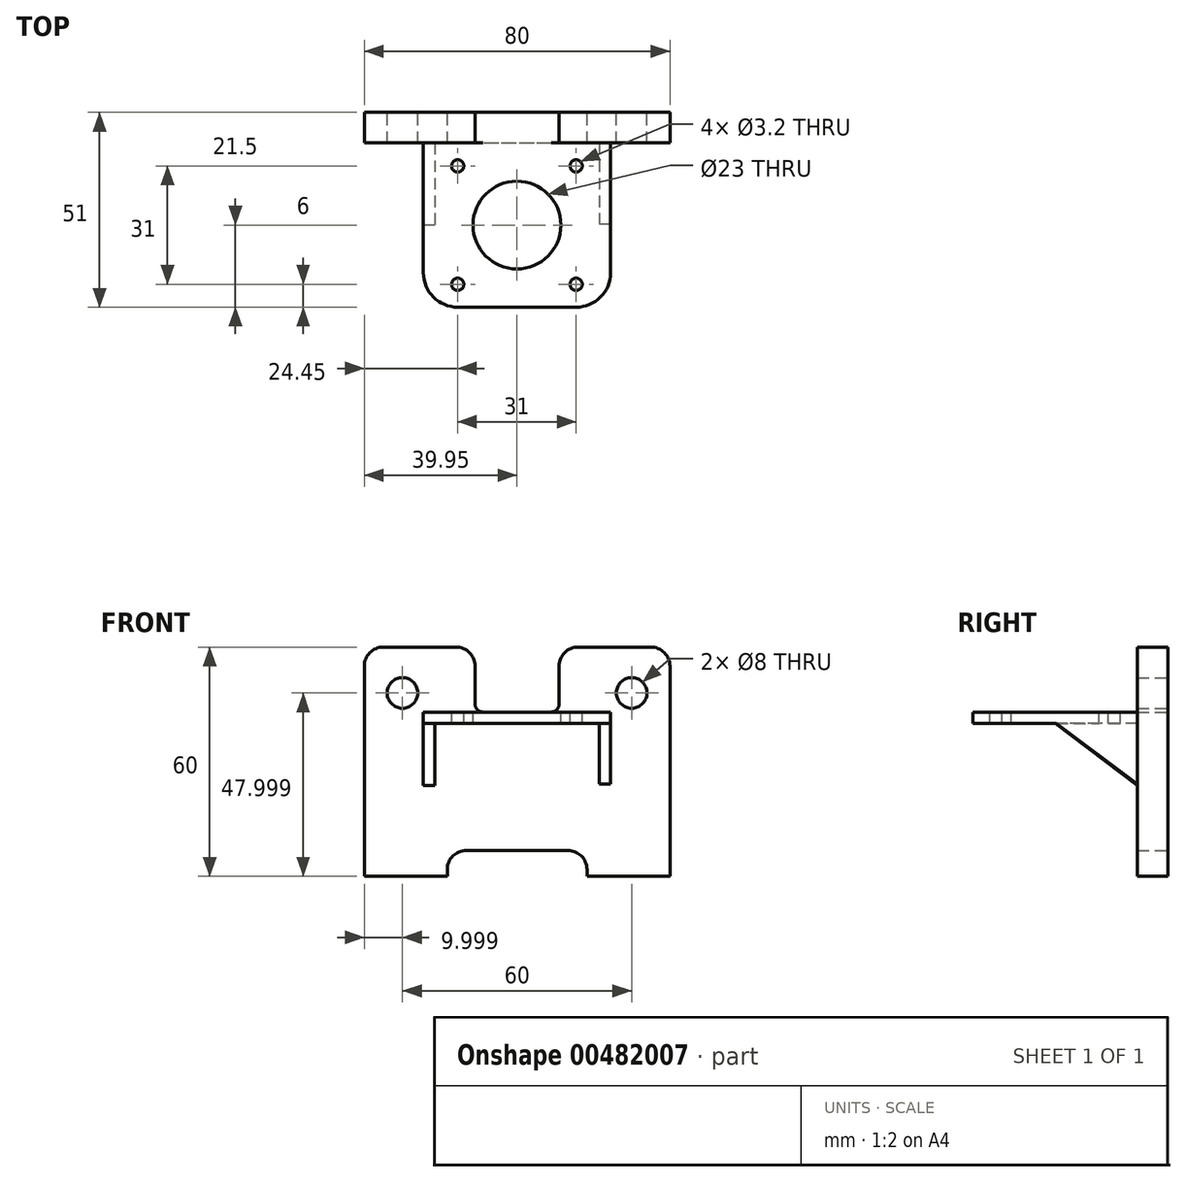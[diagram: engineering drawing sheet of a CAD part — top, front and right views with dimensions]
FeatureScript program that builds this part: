
annotation { "Feature Type Name" : "Feature", "Feature Type Description" : "" }
export const myFeature = defineFeature(function(context is Context, id is Id, definition is map)
    precondition{}
    {
        {
            var Q0;
            Q0=qCreatedBy(makeId("Front.planeOp"),FACE);
            var sketch = newSketch(context, id + "F0", { "sketchPlane" : qUnion([Q0])});
            skLineSegment(sketch, "E0", {"start": v(0.05, 175.86) * mm, "end": v(0.05, -106.38) * mm, "construction": true});
            skLineSegment(sketch, "E1.bottom", {"start": v(-34.95, 58.36) * mm, "end": v(-15.95, 58.36) * mm});
            skLineSegment(sketch, "E1.top", {"start": v(-39.95, -1.64) * mm, "end": v(-18.24, -1.64) * mm});
            skLineSegment(sketch, "E1.left", {"start": v(-39.95, 53.36) * mm, "end": v(-39.95, -1.64) * mm});
            skLineSegment(sketch, "E1.right", {"start": v(40.05, 53.36) * mm, "end": v(40.05, -1.64) * mm});
            skPoint(sketch, "E1.middle", {"position": v(0.05, 28.36) * mm});
            skCircle(sketch, "E2", {"center": v(-29.95, 46.36) * mm, "radius": 4 * mm});
            skCircle(sketch, "E3", {"center": v(30.05, 46.36) * mm, "radius": 4 * mm});
            skCircle(sketch, "E4", {"center": v(-29.95, 10.36) * mm, "radius": 5 * mm});
            skCircle(sketch, "E5", {"center": v(30.05, 10.36) * mm, "radius": 5 * mm});
            skPoint(sketch, "E6.visualSharp", {"position": v(-39.95, 58.36) * mm});
            skArc(sketch, "E6.filletArc", {"start": v(-34.95, 58.36) * mm, "mid": v(-38.49, 56.9) * mm, "end": v(-39.95, 53.36) * mm});
            skPoint(sketch, "E7.visualSharp", {"position": v(40.05, 58.36) * mm});
            skArc(sketch, "E7.filletArc", {"start": v(40.05, 53.36) * mm, "mid": v(38.58, 56.9) * mm, "end": v(35.05, 58.36) * mm});
            skLineSegment(sketch, "E8.top", {"start": v(-8.95, 41.36) * mm, "end": v(9.05, 41.36) * mm});
            skLineSegment(sketch, "E8.left", {"start": v(-10.95, 53.36) * mm, "end": v(-10.95, 43.36) * mm});
            skLineSegment(sketch, "E8.right", {"start": v(11.05, 53.36) * mm, "end": v(11.05, 43.36) * mm});
            skPoint(sketch, "E8.middle", {"position": v(0.05, 49.86) * mm});
            skPoint(sketch, "E9.visualSharp", {"position": v(11.05, 41.36) * mm});
            skArc(sketch, "E9.filletArc", {"start": v(9.05, 41.36) * mm, "mid": v(10.46, 41.94) * mm, "end": v(11.05, 43.36) * mm});
            skPoint(sketch, "E10.visualSharp", {"position": v(-10.95, 41.36) * mm});
            skArc(sketch, "E10.filletArc", {"start": v(-10.95, 43.36) * mm, "mid": v(-10.37, 41.94) * mm, "end": v(-8.95, 41.36) * mm});
            skLineSegment(sketch, "E11.trimOffspring", {"start": v(16.05, 58.36) * mm, "end": v(35.05, 58.36) * mm});
            skPoint(sketch, "E12.visualSharp", {"position": v(-10.95, 58.36) * mm});
            skArc(sketch, "E12.filletArc", {"start": v(-10.95, 53.36) * mm, "mid": v(-12.42, 56.9) * mm, "end": v(-15.95, 58.36) * mm});
            skPoint(sketch, "E13.visualSharp", {"position": v(11.05, 58.36) * mm});
            skArc(sketch, "E13.filletArc", {"start": v(16.05, 58.36) * mm, "mid": v(12.51, 56.9) * mm, "end": v(11.05, 53.36) * mm});
            skLineSegment(sketch, "E14.top", {"start": v(-13.24, 5.13) * mm, "end": v(13.34, 5.13) * mm});
            skLineSegment(sketch, "E14.left", {"start": v(-18.24, -1.64) * mm, "end": v(-18.24, 0.13) * mm});
            skLineSegment(sketch, "E14.right", {"start": v(18.34, -1.64) * mm, "end": v(18.34, 0.13) * mm});
            skPoint(sketch, "E14.middle", {"position": v(0.05, 1.74) * mm});
            skLineSegment(sketch, "E15.trimOffspring", {"start": v(18.34, -1.64) * mm, "end": v(40.05, -1.64) * mm});
            skPoint(sketch, "E16.visualSharp", {"position": v(-18.24, 5.13) * mm});
            skArc(sketch, "E16.filletArc", {"start": v(-13.24, 5.13) * mm, "mid": v(-16.77, 3.66) * mm, "end": v(-18.24, 0.13) * mm});
            skPoint(sketch, "E17.visualSharp", {"position": v(18.34, 5.13) * mm});
            skArc(sketch, "E17.filletArc", {"start": v(18.34, 0.13) * mm, "mid": v(16.87, 3.66) * mm, "end": v(13.34, 5.13) * mm});
            skLineSegment(sketch, "E18", {"start": v(18.34, -1.64) * mm, "end": v(-18.24, -1.64) * mm});
            skSolve(sketch);
        }
        {
            var Q0;
            Q0=makeQuery(id+"F0.imprint","IMPRINT",FACE,{"disambiguationData":[TD([[makeQuery(id+"F0.imprint","IMPRINT",EDGE,{"derivedFrom":sQuery(id+"F0.wireOp",EDGE,"E1.top")}),1.0]])]});
            extrude(context, id + "F1", {"entities" : qUnion([Q0]), "depth" : 8 * mm});
        }
        {
            var Q0;
            Q0=makeQuery(id+"F1.opExtrude","SWEPT_FACE",FACE,{"disambiguationData":[OSD([sQuery(id+"F0.wireOp",EDGE,"E8.top")])]});
            var sketch = newSketch(context, id + "F2", { "sketchPlane" : qUnion([Q0])});
            skLineSegment(sketch, "E19.bottom", {"start": v(-24.49, -8) * mm, "end": v(24.51, -8) * mm});
            skLineSegment(sketch, "E19.top", {"start": v(-24.49, -51) * mm, "end": v(24.51, -51) * mm});
            skLineSegment(sketch, "E19.left", {"start": v(-24.49, -8) * mm, "end": v(-24.49, -51) * mm});
            skLineSegment(sketch, "E19.right", {"start": v(24.51, -8) * mm, "end": v(24.51, -51) * mm});
            skCircle(sketch, "E20", {"center": v(0, -29.5) * mm, "radius": 11.5 * mm});
            skPoint(sketch, "E20.centerSnap0", {"position": v(-24.49, -29.5) * mm});
            skCircle(sketch, "E21", {"center": v(-15.5, -45) * mm, "radius": 1.6 * mm});
            skCircle(sketch, "E22", {"center": v(15.5, -45) * mm, "radius": 1.6 * mm});
            skCircle(sketch, "E23", {"center": v(15.5, -14) * mm, "radius": 1.6 * mm});
            skCircle(sketch, "E24", {"center": v(-15.5, -14) * mm, "radius": 1.6 * mm});
            skLineSegment(sketch, "E25", {"start": v(-37.4, -29.5) * mm, "end": v(46.63, -29.5) * mm, "construction": true});
            skPoint(sketch, "E25.endSnap0", {"position": v(24.51, -29.5) * mm});
            skLineSegment(sketch, "E26", {"start": v(0, -70.53) * mm, "end": v(0, 44.03) * mm, "construction": true});
            skSolve(sketch);
        }
        {
            var Q0;
            Q0=qSketchRegion(id+"F2",true);
            extrude(context, id + "F3", {"entities" : qUnion([Q0]), "operationType" : NewBodyOperationType.ADD, "oppositeDirection" : true, "depth" : 3 * mm});
        }
        {
            var Q0;
            Q0=makeQuery(id+"F3.opExtrude","SWEPT_FACE",FACE,{"disambiguationData":[OSD([sQuery(id+"F2.wireOp",EDGE,"E19.left")])]});
            var sketch = newSketch(context, id + "F4", { "sketchPlane" : qUnion([Q0])});
            skLineSegment(sketch, "E27", {"start": v(8, 38.36) * mm, "end": v(29.5, 38.36) * mm});
            skLineSegment(sketch, "E28", {"start": v(29.5, 38.36) * mm, "end": v(7.88, 22.06) * mm});
            skLineSegment(sketch, "E29", {"start": v(7.88, 22.06) * mm, "end": v(8, 38.36) * mm});
            skSolve(sketch);
        }
        {
            var Q0;
            Q0=qSketchRegion(id+"F4",true);
            extrude(context, id + "F5", {"entities" : qUnion([Q0]), "operationType" : NewBodyOperationType.ADD, "oppositeDirection" : true, "depth" : 3 * mm});
        }
        {
            var Q0;
            Q0=makeQuery(id+"F3.opExtrude","SWEPT_EDGE",EDGE,{"disambiguationData":[OSD([sQuery(id+"F2.wireOp",EDGE,"E19.top"),sQuery(id+"F2.wireOp",EDGE,"E19.left")])]});
            var Q1;
            Q1=makeQuery(id+"F3.opExtrude","SWEPT_EDGE",EDGE,{"disambiguationData":[OSD([sQuery(id+"F2.wireOp",EDGE,"E19.top"),sQuery(id+"F2.wireOp",EDGE,"E19.right")])]});
            fillet(context, id + "F6", {"entities" : qUnion([Q0, Q1]), "radius" : 9 * mm, "tangentPropagation" : true, "allowEdgeOverflow" : false});
        }
        {
            var Q0;
            Q0=makeQuery(id+"F3.opExtrude","SWEPT_FACE",FACE,{"disambiguationData":[OSD([sQuery(id+"F2.wireOp",EDGE,"E19.right")])]});
            var sketch = newSketch(context, id + "F7", { "sketchPlane" : qUnion([Q0])});
            skLineSegment(sketch, "E30", {"start": v(-29.19, 38.36) * mm, "end": v(-8, 38.36) * mm});
            skLineSegment(sketch, "E31", {"start": v(-8, 38.36) * mm, "end": v(-8, 22.56) * mm});
            skLineSegment(sketch, "E32", {"start": v(-8, 22.56) * mm, "end": v(-29.19, 38.36) * mm});
            skSolve(sketch);
        }
        {
            var Q0;
            Q0=qSketchRegion(id+"F7",true);
            extrude(context, id + "F8", {"entities" : qUnion([Q0]), "operationType" : NewBodyOperationType.ADD, "oppositeDirection" : true, "depth" : 3 * mm});
        }
        {
            var Q0;
            Q0=makeQuery(id+"F0.imprint","IMPRINT",FACE,{"disambiguationData":[TD([[makeQuery(id+"F0.imprint","IMPRINT",EDGE,{"derivedFrom":sQuery(id+"F0.wireOp",EDGE,"E5")}),1.0]])]});
            var Q1;
            Q1=makeQuery(id+"F0.imprint","IMPRINT",FACE,{"disambiguationData":[TD([[makeQuery(id+"F0.imprint","IMPRINT",EDGE,{"derivedFrom":sQuery(id+"F0.wireOp",EDGE,"E4")}),1.0]])]});
            extrude(context, id + "F9", {"entities" : qUnion([Q0, Q1]), "operationType" : NewBodyOperationType.ADD, "depth" : 8 * mm});
        }
        {
            var Q0;
            Q0=makeQuery(id+"F1.opExtrude","SWEPT_BODY",BODY,{"disambiguationData":[OSD([sQuery(id+"F0.wireOp",EDGE,"E1.bottom"),sQuery(id+"F0.wireOp",EDGE,"E1.top"),sQuery(id+"F0.wireOp",EDGE,"E1.left"),sQuery(id+"F0.wireOp",EDGE,"E1.right"),sQuery(id+"F0.wireOp",EDGE,"E2"),sQuery(id+"F0.wireOp",EDGE,"E3"),sQuery(id+"F0.wireOp",EDGE,"E4"),sQuery(id+"F0.wireOp",EDGE,"E5"),sQuery(id+"F0.wireOp",EDGE,"E6.filletArc"),sQuery(id+"F0.wireOp",EDGE,"E7.filletArc"),sQuery(id+"F0.wireOp",EDGE,"E8.top"),sQuery(id+"F0.wireOp",EDGE,"E8.left"),sQuery(id+"F0.wireOp",EDGE,"E8.right"),sQuery(id+"F0.wireOp",EDGE,"E9.filletArc"),sQuery(id+"F0.wireOp",EDGE,"E10.filletArc"),sQuery(id+"F0.wireOp",EDGE,"E11.trimOffspring"),sQuery(id+"F0.wireOp",EDGE,"E12.filletArc"),sQuery(id+"F0.wireOp",EDGE,"E13.filletArc"),sQuery(id+"F0.wireOp",EDGE,"E14.top"),sQuery(id+"F0.wireOp",EDGE,"E14.left"),sQuery(id+"F0.wireOp",EDGE,"E14.right"),sQuery(id+"F0.wireOp",EDGE,"E15.trimOffspring"),sQuery(id+"F0.wireOp",EDGE,"E16.filletArc"),sQuery(id+"F0.wireOp",EDGE,"E17.filletArc"),sQuery(id+"F0.wireOp",EDGE,"KRNpDy01-qwSV-cn72-EpMy-D93mMohE8gNb")])]});
            transform(context, id + "F10", {"entities" : qUnion([Q0]), "transformType" : TransformType.TRANSLATION_3D, "dx" : 0 * mm, "dy" : 0 * mm, "dz" : 0 * mm, "makeCopy" : true});
        }
        {
            var Q0;
            {var subQ0=sQuery(id+"F0.wireOp",EDGE,"KRNpDy01-qwSV-cn72-EpMy-D93mMohE8gNb");var subQ1=sQuery(id+"F0.wireOp",EDGE,"E14.top");var subQ2=makeQuery(id+"F0.imprint","INTERSECT",VERTEX,{"disambiguationData":[OD(0.0)],"derivedFrom":[subQ1,subQ0]});Q0=makeQuery(id+"F0.imprint","IMPRINT",FACE,{"disambiguationData":[TD([[makeQuery(id+"F0.imprint","IMPRINT",EDGE,{"disambiguationData":[TD([[subQ2,-1.0]])],"derivedFrom":subQ1}),1.0]])]});}
            extrude(context, id + "F11", {"entities" : qUnion([Q0]), "depth" : 8 * mm});
        }
        {
            var Q0;
            Q0=makeQuery(id+"F11.opExtrude","SWEPT_BODY",BODY,{"disambiguationData":[OSD([sQuery(id+"F0.wireOp",EDGE,"E14.top"),sQuery(id+"F0.wireOp",EDGE,"KRNpDy01-qwSV-cn72-EpMy-D93mMohE8gNb")])]});
            deleteBodies(context, id + "F12", {"entities" : qUnion([Q0])});
        }
        {
            var Q0;
            Q0=makeQuery(id+"F10.opPattern","COPY",BODY,{"derivedFrom":makeQuery(id+"F1.opExtrude","SWEPT_BODY",BODY,{"disambiguationData":[OSD([sQuery(id+"F0.wireOp",EDGE,"E1.bottom"),sQuery(id+"F0.wireOp",EDGE,"E1.top"),sQuery(id+"F0.wireOp",EDGE,"E1.left"),sQuery(id+"F0.wireOp",EDGE,"E1.right"),sQuery(id+"F0.wireOp",EDGE,"E2"),sQuery(id+"F0.wireOp",EDGE,"E3"),sQuery(id+"F0.wireOp",EDGE,"E4"),sQuery(id+"F0.wireOp",EDGE,"E5"),sQuery(id+"F0.wireOp",EDGE,"E6.filletArc"),sQuery(id+"F0.wireOp",EDGE,"E7.filletArc"),sQuery(id+"F0.wireOp",EDGE,"E8.top"),sQuery(id+"F0.wireOp",EDGE,"E8.left"),sQuery(id+"F0.wireOp",EDGE,"E8.right"),sQuery(id+"F0.wireOp",EDGE,"E9.filletArc"),sQuery(id+"F0.wireOp",EDGE,"E10.filletArc"),sQuery(id+"F0.wireOp",EDGE,"E11.trimOffspring"),sQuery(id+"F0.wireOp",EDGE,"E12.filletArc"),sQuery(id+"F0.wireOp",EDGE,"E13.filletArc"),sQuery(id+"F0.wireOp",EDGE,"E14.top"),sQuery(id+"F0.wireOp",EDGE,"E14.left"),sQuery(id+"F0.wireOp",EDGE,"E14.right"),sQuery(id+"F0.wireOp",EDGE,"E15.trimOffspring"),sQuery(id+"F0.wireOp",EDGE,"E16.filletArc"),sQuery(id+"F0.wireOp",EDGE,"E17.filletArc"),sQuery(id+"F0.wireOp",EDGE,"KRNpDy01-qwSV-cn72-EpMy-D93mMohE8gNb")])]}),"instanceName":"1"});
            deleteBodies(context, id + "F13", {"entities" : qUnion([Q0])});
        }
    });
